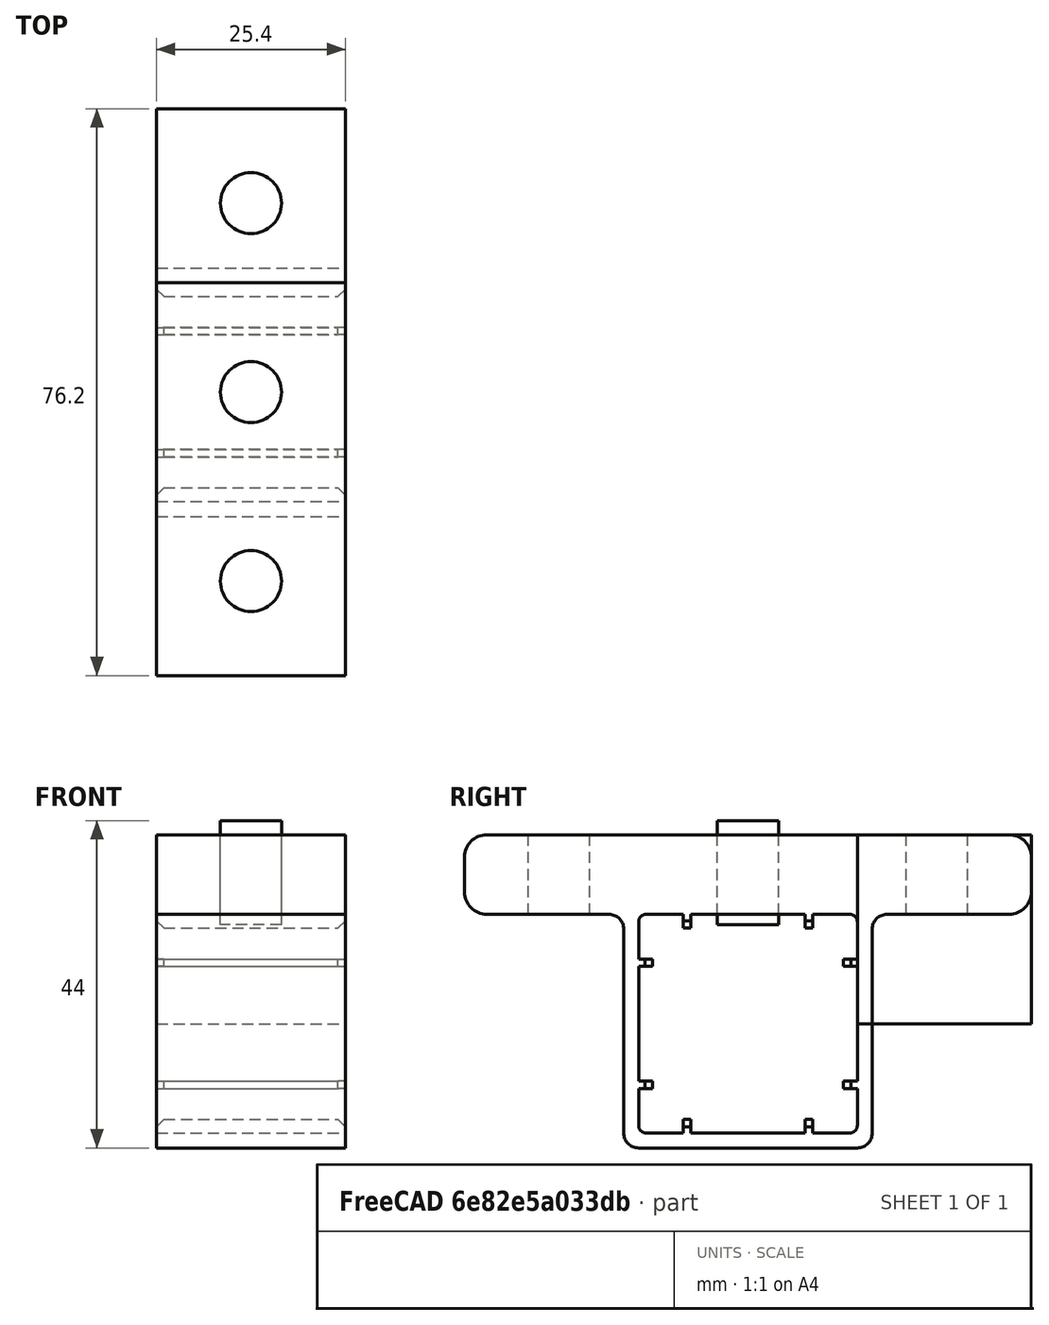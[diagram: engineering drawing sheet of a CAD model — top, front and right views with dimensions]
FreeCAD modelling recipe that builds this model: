
FCSTD DOCUMENT  (FreeCAD 0.16RUnknown)
Label: linear-bearing
License: All rights reserved
LicenseURL: http://en.wikipedia.org/wiki/All_rights_reserved
objects: Part::Box×12, PartDesign::Fillet×4, Part::Cut×3, Part::Cylinder×3, Part::MultiFuse×2, PartDesign::Chamfer×1
note: 25 computed .brp shape members not serialized (recipe doc carries the construction recipe); baked Part::Feature solids carry a one-line shape summary decoded from their .brp

FEATURE [Part::Box] Box  label="Cube"
  Height = 29.4
  Length = 52
  Placement = pos=(-1,2,2) rot=(0,0,1;0rad)
  Width = 29.4
FEATURE [Part::Box] Box001  label="Cube001"
  Height = 33.4
  Length = 25.4
  Width = 33.4
FEATURE [PartDesign::Fillet] Fillet
  Base = -> Box001 [Edge11,Edge9,Edge10,Edge12]
  Radius = 2
FEATURE [PartDesign::Fillet] Fillet001
  Base = -> Box [Edge10,Edge9,Edge12,Edge11]
  Placement = pos=(-1,2,2) rot=(0,0,1;0rad)
  Radius = 1
FEATURE [Part::Cut] Cut
  Base = -> Fillet
  Tool = -> Fillet001
FEATURE [Part::Box] Box002  label="Cube002"
  Height = 1
  Length = 25.4
  Placement = pos=(0,0,8) rot=(0,0,1;0rad)
  Width = 3.85
FEATURE [Part::Box] Box003  label="Cube003"
  Height = 1
  Length = 25.4
  Placement = pos=(0,0,24.4) rot=(0,0,1;0rad)
  Width = 3.85
FEATURE [Part::Box] Box004  label="Cube004"
  Height = 1
  Length = 25.4
  Placement = pos=(0,29.55,8) rot=(0,0,1;0rad)
  Width = 3.85
FEATURE [Part::Box] Box005  label="Cube005"
  Height = 1
  Length = 25.4
  Placement = pos=(0,29.55,24.4) rot=(0,0,1;0rad)
  Width = 3.85
FEATURE [Part::Box] Box006  label="Cube006"
  Height = 3.85
  Length = 25.4
  Placement = pos=(0,8,0) rot=(0,0,1;0rad)
  Width = 1
FEATURE [Part::Box] Box007  label="Cube007"
  Height = 3.85
  Length = 25.4
  Placement = pos=(0,24.4,0) rot=(0,0,1;0rad)
  Width = 1
FEATURE [Part::Box] Box008  label="Cube008"
  Height = 3.85
  Length = 25.4
  Placement = pos=(0,24.4,29.55) rot=(0,0,1;0rad)
  Width = 1
FEATURE [Part::Box] Box009  label="Cube009"
  Height = 3.85
  Length = 25.4
  Placement = pos=(0,8,29.55) rot=(0,0,1;0rad)
  Width = 1
FEATURE [Part::Box] Box010  label="Cube010"
  Height = 10.7
  Length = 25.4
  Placement = pos=(0,-21.4,31.4) rot=(0,0,1;0rad)
  Width = 76.2
FEATURE [Part::Box] Box011  label="Cube011"
  Height = 25.4
  Length = 25.4
  Placement = pos=(0,31.4,16.7) rot=(0,0,1;0rad)
  Width = 23.4
FEATURE [Part::Cylinder] Cylinder
  Angle = 360
  Height = 14
  Placement = pos=(12.7,42.1,30) rot=(0,0,1;0rad)
  Radius = 4.1
FEATURE [Part::Cylinder] Cylinder001
  Angle = 360
  Height = 14
  Placement = pos=(12.7,16.7,30) rot=(0,0,1;0rad)
  Radius = 4.1
FEATURE [Part::Cylinder] Cylinder002
  Angle = 360
  Height = 14
  Placement = pos=(12.7,-8.7,30) rot=(0,0,1;0rad)
  Radius = 4.1
FEATURE [Part::MultiFuse] Fusion
  Shapes = -> [Cut,Box010]
FEATURE [PartDesign::Fillet] Fillet002
  Base = -> Fusion [Edge21,Edge25]
  Radius = 2
FEATURE [PartDesign::Fillet] Fillet003
  Base = -> Fillet002 [Edge35,Edge34,Edge12,Edge31]
  Radius = 3
FEATURE [Part::Cut] Cut001
  Base = -> Fillet003
  Tool = -> Cylinder002
FEATURE [Part::Cut] Cut002
  Base = -> Cut001
  Tool = -> Cylinder
FEATURE [Part::MultiFuse] Fusion001
  Shapes = -> [Cut002,Box004,Box007,Box006,Box002,Box003,Box009,Box008,Box005]
FEATURE [PartDesign::Chamfer] Chamfer
  Base = -> Fusion001 [Edge176,Edge214,Edge269,Edge252,Edge199,Edge55,Edge2,Edge169,Edge53,Edge208,Edge264,Edge271,Edge220,Edge191,Edge187,Edge4]
  Size = 1
